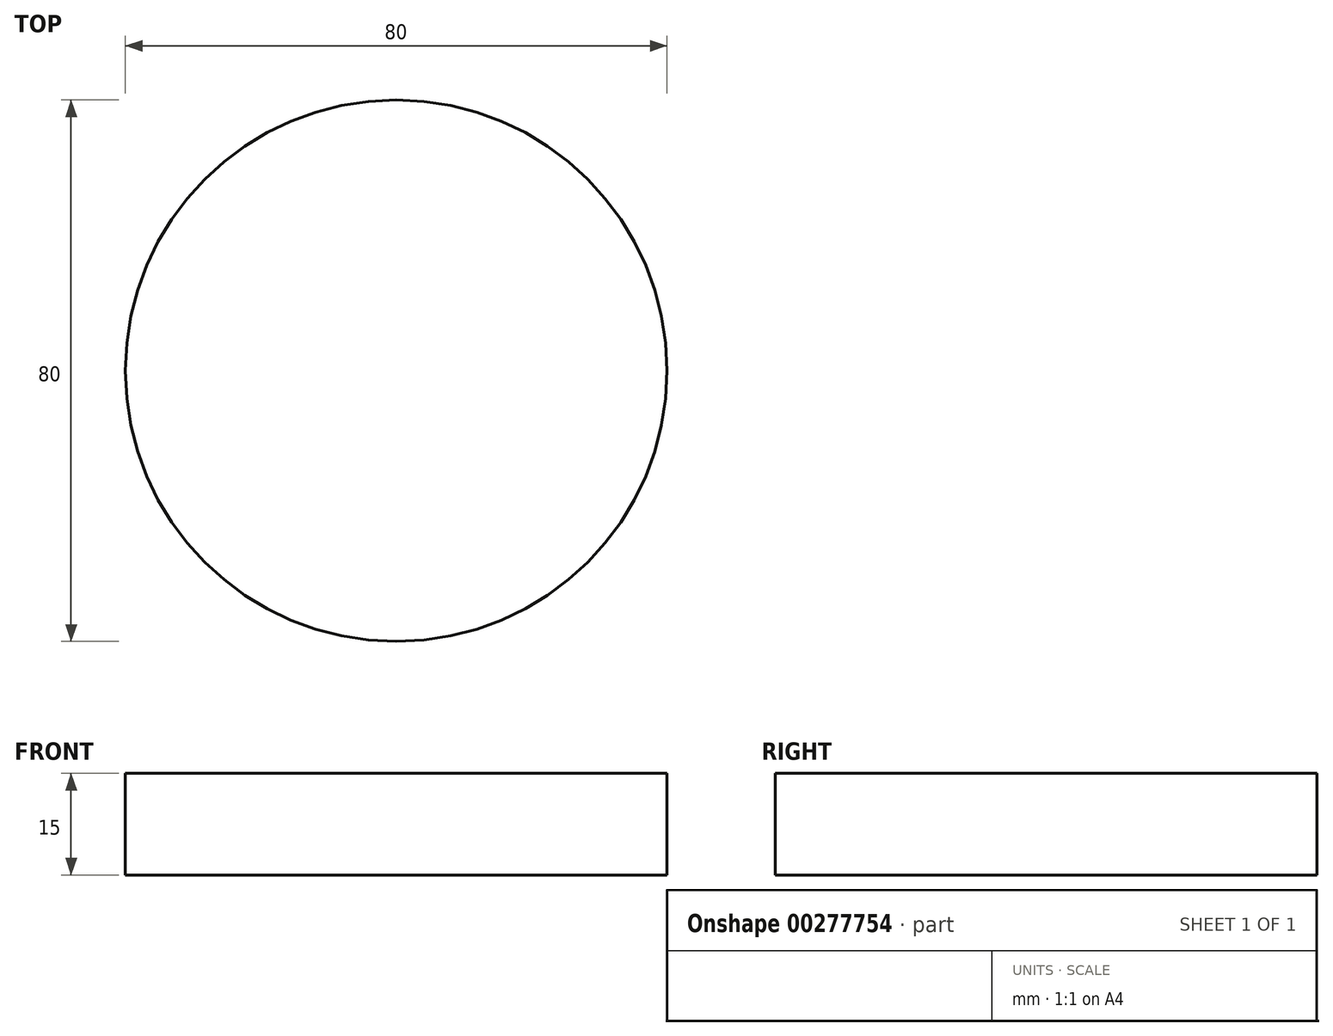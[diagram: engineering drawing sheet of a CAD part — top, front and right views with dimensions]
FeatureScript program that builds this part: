
annotation { "Feature Type Name" : "Feature", "Feature Type Description" : "" }
export const myFeature = defineFeature(function(context is Context, id is Id, definition is map)
    precondition{}
    {
        {
            var Q0;
            Q0=qCreatedBy(makeId("Top.planeOp"),FACE);
            var sketch = newSketch(context, id + "F0", { "sketchPlane" : qUnion([Q0])});
            skCircle(sketch, "E0", {"center": v(0, 0) * mm, "radius": 40 * mm});
            skSolve(sketch);
        }
        {
            var Q0;
            Q0 = qSketchRegion(id + "F0", true);
            extrude(context, id + "F1", {"entities" : qUnion([Q0]), "depth" : 15 * mm});
        }
    });
